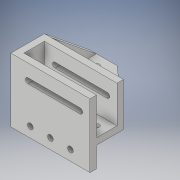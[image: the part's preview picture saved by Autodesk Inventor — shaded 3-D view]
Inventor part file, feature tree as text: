
AUTODESK INVENTOR PART (.ipt)
format: ipt  version: 2019 (Build 230136000, 136)  size: 208,384 bytes
history: native  units: in
note: dims shown in document units (in); Inventor stores cm internally (conversion verified against a paired STEP export)
features: extrude x7, sketch x7, plane x1, projected_geometry x1
ambient origin geometry x8: Origin, YZ Plane, XZ Plane, XY Plane, X Axis, Y Axis, Z Axis, Center Point
bodies: Solid1 (feature_tree)
feature tree (16):
  extrude  "Extrusion1"  Depth=0.7874in
  extrude  "Extrusion2"  Depth=0.25in
  extrude  "Extrusion3"  Depth=2.4528in TaperAngle=0.0deg
  plane  "Work Plane1"
  extrude  "Extrusion4"  Depth=0.7874in
  extrude  "Extrusion5"  Depth=0.3937in
  extrude  "Extrusion6"  Depth=0.3937in
  extrude  "Extrusion7"  Depth=0.25in
  sketch  "Sketch1"  dims[d0=2.0in d1=0.7874in]
  sketch  "Sketch2"  dims[d2=0.7874in d3=0.25in]
  sketch  "Sketch3"  dims[d4=0.25in d5=2.4528in d6=0.0in]
  sketch  "Sketch4"  dims[d7=0.7874in d8=0.2165in]
  projected_geometry  "Projected Loop1"
  sketch  "Sketch5"  dims[d9=0.75in d10=1.1811in d12=0.7687in d13=0.3937in d15=1.0in]
  sketch  "Sketch6"  dims[d17=2.4528in d18=0.0in d19=0.3937in]
  sketch  "Sketch7"  dims[d20=0.2165in d21=0.75in d22=1.1811in d24=0.7687in d25=0.3937in d27=1.0in d29=2.4528in d30=0.0in d31=-0.7874in d32=0.7874in d33=1.1811in d35=1.0in d36=0.3937in d38=1.0in d40=0.2165in d41=1.1811in d43=1.0in d44=0.3937in d46=1.0in d48=0.25in d49=0.0in d50=0.25in d51=0.25in d52=0.25in d53=0.0in d54=0.8268in d55=0.1969in d56=2.0in d57=0.25in d58=0.0in d59=0.25in d60=0.0in]
